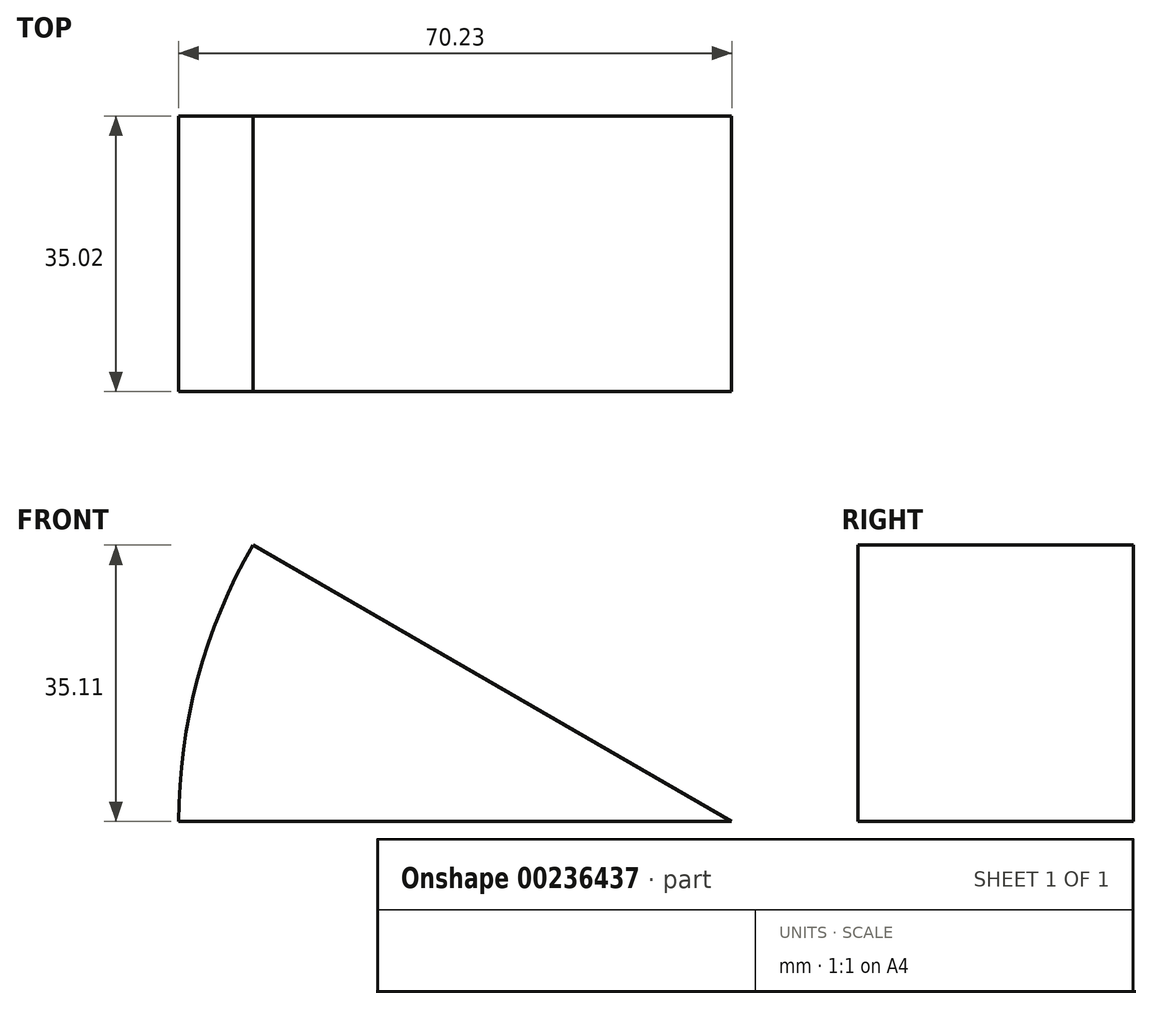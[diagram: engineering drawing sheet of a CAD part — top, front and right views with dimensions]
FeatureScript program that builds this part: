
annotation { "Feature Type Name" : "Feature", "Feature Type Description" : "" }
export const myFeature = defineFeature(function(context is Context, id is Id, definition is map)
    precondition{}
    {
        {
            var Q0;
            Q0=qCreatedBy(makeId("Top.planeOp"),FACE);
            var sketch = newSketch(context, id + "F0", { "sketchPlane" : qUnion([Q0])});
            skLineSegment(sketch, "E0.bottom", {"start": v(-45.48, 16.04) * mm, "end": v(24.75, 16.04) * mm});
            skLineSegment(sketch, "E0.top", {"start": v(-45.48, -18.98) * mm, "end": v(24.75, -18.98) * mm});
            skLineSegment(sketch, "E0.left", {"start": v(-45.48, 16.04) * mm, "end": v(-45.48, -18.98) * mm});
            skLineSegment(sketch, "E0.right", {"start": v(24.75, 16.04) * mm, "end": v(24.75, -18.98) * mm});
            skSolve(sketch);
        }
        {
            var Q0;
            Q0 = qSketchRegion(id + "F0", true);
            var Q1;
            Q1=sQuery(id+"F0.wireOp",EDGE,"E0.right");
            revolve(context, id + "F1", {"entities" : qUnion([Q0]), "axis" : qUnion([Q1]), "revolveType" : RevolveType.ONE_DIRECTION, "oppositeDirection" : true, "angle" : 30 * degree});
        }
    });
